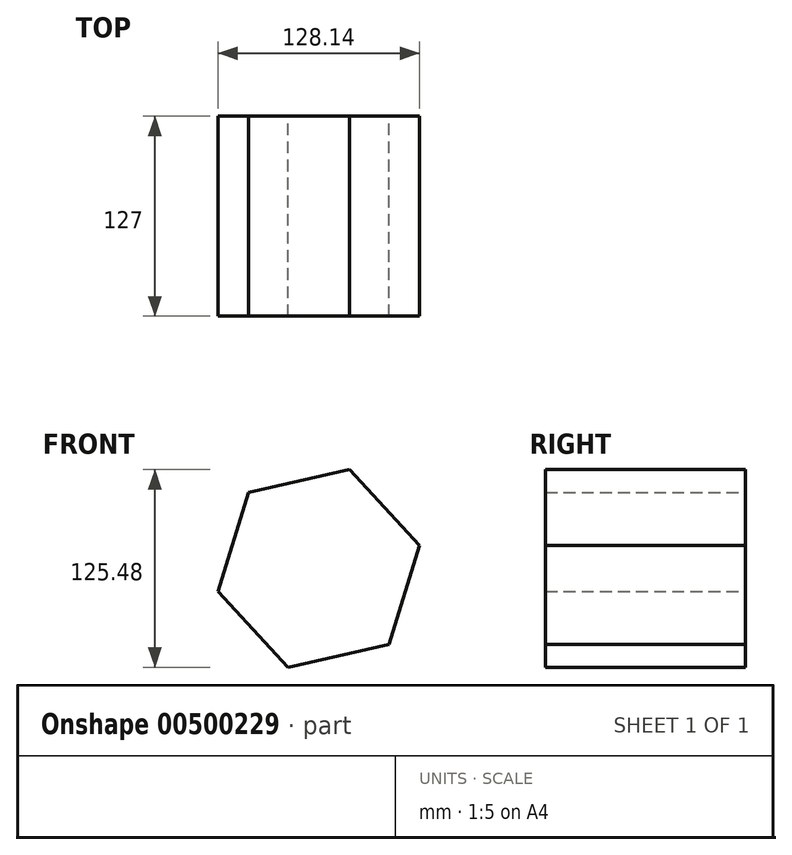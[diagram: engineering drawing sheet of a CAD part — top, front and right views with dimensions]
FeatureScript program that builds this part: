
annotation { "Feature Type Name" : "Feature", "Feature Type Description" : "" }
export const myFeature = defineFeature(function(context is Context, id is Id, definition is map)
    precondition{}
    {
        {
            var Q0;
            Q0=qCreatedBy(makeId("Front.planeOp"),FACE);
            var sketch = newSketch(context, id + "F0", { "sketchPlane" : qUnion([Q0])});
            skCircle(sketch, "E0.cCircle", {"center": v(0, 0) * mm, "radius": 65.7 * mm, "construction": true});
            skLineSegment(sketch, "E0.0", {"start": v(44.6, -48.24) * mm, "end": v(-19.48, -62.74) * mm});
            skLineSegment(sketch, "E0.1", {"start": v(-19.48, -62.74) * mm, "end": v(-64.07, -14.5) * mm});
            skLineSegment(sketch, "E0.2", {"start": v(-64.07, -14.5) * mm, "end": v(-44.6, 48.24) * mm});
            skLineSegment(sketch, "E0.3", {"start": v(-44.6, 48.24) * mm, "end": v(19.48, 62.74) * mm});
            skLineSegment(sketch, "E0.4", {"start": v(19.48, 62.74) * mm, "end": v(64.07, 14.5) * mm});
            skLineSegment(sketch, "E0.5", {"start": v(64.07, 14.5) * mm, "end": v(44.6, -48.24) * mm});
            skSolve(sketch);
        }
        {
            var Q0;
            Q0 = qSketchRegion(id + "F0", true);
            extrude(context, id + "F1", {"entities" : qUnion([Q0]), "depth" : 127 * mm});
        }
    });
